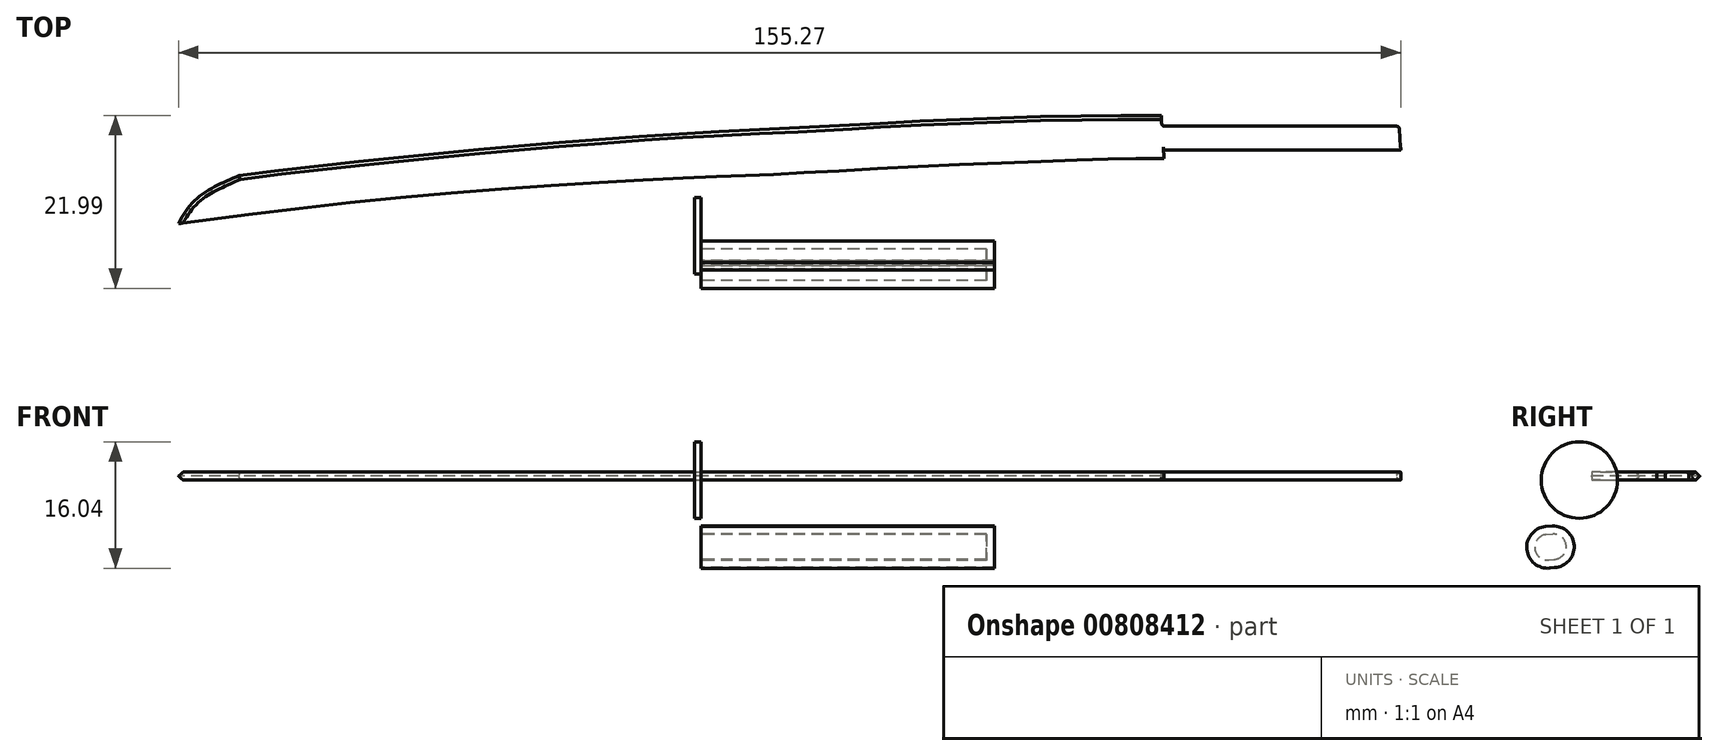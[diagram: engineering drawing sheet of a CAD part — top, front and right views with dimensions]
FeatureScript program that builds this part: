
annotation { "Feature Type Name" : "Feature", "Feature Type Description" : "" }
export const myFeature = defineFeature(function(context is Context, id is Id, definition is map)
    precondition{}
    {
        {
            var Q0;
            Q0=qCreatedBy(makeId("Top.planeOp"),FACE);
            var sketch = newSketch(context, id + "F0", { "sketchPlane" : qUnion([Q0])});
            skFitSpline(sketch, "E0", {"points": [v(-57.5, -17.88) * mm, v(-24.78, -14.56) * mm, v(0, -13.14) * mm, v(10.78, -12.67) * mm, v(28.32, -11.72) * mm, v(48.18, -10.93) * mm, v(58.8, -10.74) * mm], "startDerivative": vector(147.82, 19.28) * mm, "endDerivative": vector(83.66, 0) * mm});
            skFitSpline(sketch, "E1", {"points": [v(-57.87, -15.54) * mm, v(-25.16, -12.23) * mm, v(-0.37, -10.8) * mm, v(10.4, -10.33) * mm, v(27.95, -9.38) * mm, v(47.8, -8.6) * mm, v(58.65, -8.54) * mm], "startDerivative": vector(147.82, 19.28) * mm, "endDerivative": vector(83.66, 0) * mm});
            skFitSpline(sketch, "E2", {"points": [v(-58.85, -12.4) * mm, v(-25.2, -8.83) * mm, v(0, -6.93) * mm, v(9.76, -6.47) * mm, v(27.81, -5.5) * mm, v(47.76, -4.82) * mm, v(58.41, -4.75) * mm], "startDerivative": vector(147.82, 19.28) * mm, "endDerivative": vector(83.66, 0) * mm});
            skFitSpline(sketch, "E3", {"points": [v(-58.85, -12.4) * mm, v(-62.91, -14.35) * mm, v(-65.86, -17.07) * mm, v(-67, -19.09) * mm], "startDerivative": vector(-8.5, -4.15) * mm, "endDerivative": vector(-2.3, -5.15) * mm});
            skLineSegment(sketch, "E4", {"start": v(-57.5, -17.88) * mm, "end": v(-67, -19.09) * mm});
            skLineSegment(sketch, "E5", {"start": v(-57.87, -15.54) * mm, "end": v(-58.85, -12.4) * mm});
            skLineSegment(sketch, "E6", {"start": v(58.8, -10.74) * mm, "end": v(58.65, -8.54) * mm});
            skLineSegment(sketch, "E7", {"start": v(58.41, -4.75) * mm, "end": v(58.65, -8.54) * mm});
            skLineSegment(sketch, "E8", {"start": v(58.72, -9.64) * mm, "end": v(88.87, -9.64) * mm});
            skLineSegment(sketch, "E9", {"start": v(58.53, -6.64) * mm, "end": v(88.7, -6.64) * mm});
            skLineSegment(sketch, "E10", {"start": v(88.7, -6.64) * mm, "end": v(88.87, -9.64) * mm});
            skLineSegment(sketch, "E11", {"start": v(-57.87, -15.54) * mm, "end": v(-57.5, -17.88) * mm});
            skSolve(sketch);
        }
        {
            var Q0;
            Q0 = qSketchRegion(id + "F0", true);
            extrude(context, id + "F1", {"entities" : qUnion([Q0]), "depth" : 1.02 * mm, "offsetDistance" : 25.4 * mm});
        }
        {
            var Q0;
            Q0=makeQuery(id+"F1.opExtrude","CAP_EDGE",EDGE,{"disambiguationData":[OSD([sQuery(id+"F0.wireOp",EDGE,"E2")])],"isStart":false});
            var Q1;
            Q1=makeQuery(id+"F1.opExtrude","CAP_EDGE",EDGE,{"disambiguationData":[OSD([sQuery(id+"F0.wireOp",EDGE,"E3")])],"isStart":false});
            var Q2;
            Q2=makeQuery(id+"F1.opExtrude","CAP_EDGE",EDGE,{"disambiguationData":[OSD([sQuery(id+"F0.wireOp",EDGE,"E2")])],"isStart":true});
            var Q3;
            Q3=makeQuery(id+"F1.opExtrude","CAP_EDGE",EDGE,{"disambiguationData":[OSD([sQuery(id+"F0.wireOp",EDGE,"E3")])],"isStart":true});
            chamfer(context, id + "F2", {"entities" : qUnion([Q0, Q1, Q2, Q3]), "width" : 1.02 * mm, "tangentPropagation" : true});
        }
        {
            var Q0;
            Q0=qCreatedBy(makeId("Right.planeOp"),FACE);
            var sketch = newSketch(context, id + "F3", { "sketchPlane" : qUnion([Q0])});
            skCircle(sketch, "E12", {"center": v(-20.56, 0) * mm, "radius": 4.85 * mm});
            skSolve(sketch);
        }
        {
            var Q0;
            Q0=qCreatedBy(makeId("Right.planeOp"),FACE);
            var sketch = newSketch(context, id + "F4", { "sketchPlane" : qUnion([Q0])});
            skArc(sketch, "E13", {"start": v(-24.87, -5.9) * mm, "mid": v(-27.22, -8.82) * mm, "end": v(-24.3, -11.17) * mm});
            skArc(sketch, "E14", {"start": v(-23.7, -11.1) * mm, "mid": v(-21.2, -8.34) * mm, "end": v(-23.97, -5.85) * mm});
            skLineSegment(sketch, "E15", {"start": v(-24.87, -5.9) * mm, "end": v(-23.97, -5.85) * mm});
            skLineSegment(sketch, "E16", {"start": v(-24.3, -11.17) * mm, "end": v(-23.7, -11.1) * mm});
            skSolve(sketch);
        }
        {
            var Q0;
            Q0 = qSketchRegion(id + "F4", true);
            extrude(context, id + "F5", {"entities" : qUnion([Q0]), "depth" : 37.24 * mm, "offsetDistance" : 25.4 * mm});
        }
        {
            var Q0;
            Q0=makeQuery(id+"F5.opExtrude","CAP_FACE",FACE,{"disambiguationData":[OSD([sQuery(id+"F4.wireOp",EDGE,"E13"),sQuery(id+"F4.wireOp",EDGE,"E14"),sQuery(id+"F4.wireOp",EDGE,"E15"),sQuery(id+"F4.wireOp",EDGE,"E16")])],"isStart":true});
            shell(context, id + "F6", {"entities" : qUnion([Q0]), "thickness" : 1.02 * mm});
        }
        {
            var Q0;
            Q0=makeQuery(id+"F1.opExtrude","CAP_EDGE",EDGE,{"disambiguationData":[OSD([sQuery(id+"F0.wireOp",EDGE,"E8")])],"isStart":true});
            var Q1;
            Q1=makeQuery(id+"F1.opExtrude","CAP_EDGE",EDGE,{"disambiguationData":[OSD([sQuery(id+"F0.wireOp",EDGE,"E8")])],"isStart":false});
            var Q2;
            Q2=makeQuery(id+"F1.opExtrude","CAP_EDGE",EDGE,{"disambiguationData":[OSD([sQuery(id+"F0.wireOp",EDGE,"E9")])],"isStart":true});
            var Q3;
            Q3=makeQuery(id+"F1.opExtrude","SWEPT_FACE",FACE,{"disambiguationData":[OSD([sQuery(id+"F0.wireOp",EDGE,"E9")])]});
            fillet(context, id + "F7", {"entities" : qUnion([Q0, Q1, Q2, Q3]), "radius" : 0.37 * mm, "tangentPropagation" : true, "allowEdgeOverflow" : false});
        }
        {
            var Q0;
            Q0=makeQuery(id+"F3.imprint","IMPRINT",FACE,{"disambiguationData":[TD([[makeQuery(id+"F3.imprint","IMPRINT",EDGE,{"derivedFrom":sQuery(id+"F3.wireOp",EDGE,"E12")}),1.0]])]});
            extrude(context, id + "F8", {"entities" : qUnion([Q0]), "oppositeDirection" : true, "depth" : 0.81 * mm, "offsetDistance" : 25.4 * mm});
        }
    });
